# Revit family: 41. Plumbing_Fixtures_Grohe_Minta_Sink_Mixer_32488000_14_METRIC
name_source: partatom
category: Plumbing Fixtures
revit_build: Autodesk Revit 2014 (Build: 20130308_1515(x64)
units: mm (PartAtom-declared; Revit-internal decimal feet)

## types (1)
- 41. Plumbing_Fixtures_Grohe_Minta_Sink_Mixer_32488000_14_METRIC
    ADA Compliant = Yes
    Assembly Code = C1030220
    AssetType = Fixed
    Barcode = 0
    CW Connection = Yes
    CWFU = 4.5
    ClassificationName = Uniclass 2015
    ClassificationValue = Pr_40_20_87_98
    Cold Water Conection Diamiter = 10 mm  [stored 0.0328084 ft]
    Cold Water Radius = 5 mm  [stored 0.0164042 ft]
    Control Handle = Yes
    Control Handle Center = Yes
    Cost = 0 $
    Default Elevation = 600 mm
    Description = Minta Sink Mixer 1/2"
    DocumentationInstallationGuide = https://specifi.bimstore.co.uk
    DocumentationMaintenance = https://specifi.bimstore.co.uk
    DocumentationTechnical = https://specifi.bimstore.co.uk
    DurationUnit = Years
    Ecojoy = No
    ExpectedLife = 0
    Faucet Material = Grohe-Chrome
    Flow Rate = 9L/min
    HW Connection = Yes
    HWFU = 4.5
    Height = 384 mm  [stored 1.25984 ft]
    Hot Water Conection Diamiter = 10 mm  [stored 0.0328084 ft]
    Hot Water Radius = 5 mm  [stored 0.0164042 ft]
    Keynote = N13
    Length = 218 mm  [stored 0.715223 ft]
    Low Emitting Material = Yes
    Manufacturer = Grohe AG
    Mixing Leaver = Yes
    Model = Minta Sink Mixer 1/2"
    NBSObjectName = Water supply fittings for wash basins and troughs
    NBSReference = 45-35-70/371
    Name = Minta Sink Mixer 1/2"
    No of Holes = 1
    Operating Pressure = 3 bar
    Percentage of Recycled Content = 0
    Pull out or Pull Down = Pull Out
    SerialNumber = 0
    TagNumber = 0
    Tap Overhang = 223 mm  [stored 0.731627 ft]
    Type Comments = Minta Sink Mixer 1/2"
    TypeName = Minta Sink Mixer 1/2"
    URL = www.grohe.com
    Valve Spacing = 34 mm
    Vent Connection = No
    WFU = 0
    WarrantyDurationUnit = Years
    Waste Connection = No
    Width = 167 mm  [stored 0.5479 ft]
    _BIMspec_GUID = 0
    _current revision = 1
    _distributed by = www.bimstore.co.uk

note: [stored X ft] marks values corroborated as IEEE doubles in the binary element streams (Revit-internal decimal feet)

## geometry (parser evidence)
native form markers: Blend x6, Sweep x1
no freeform markers — native parametric forms only
